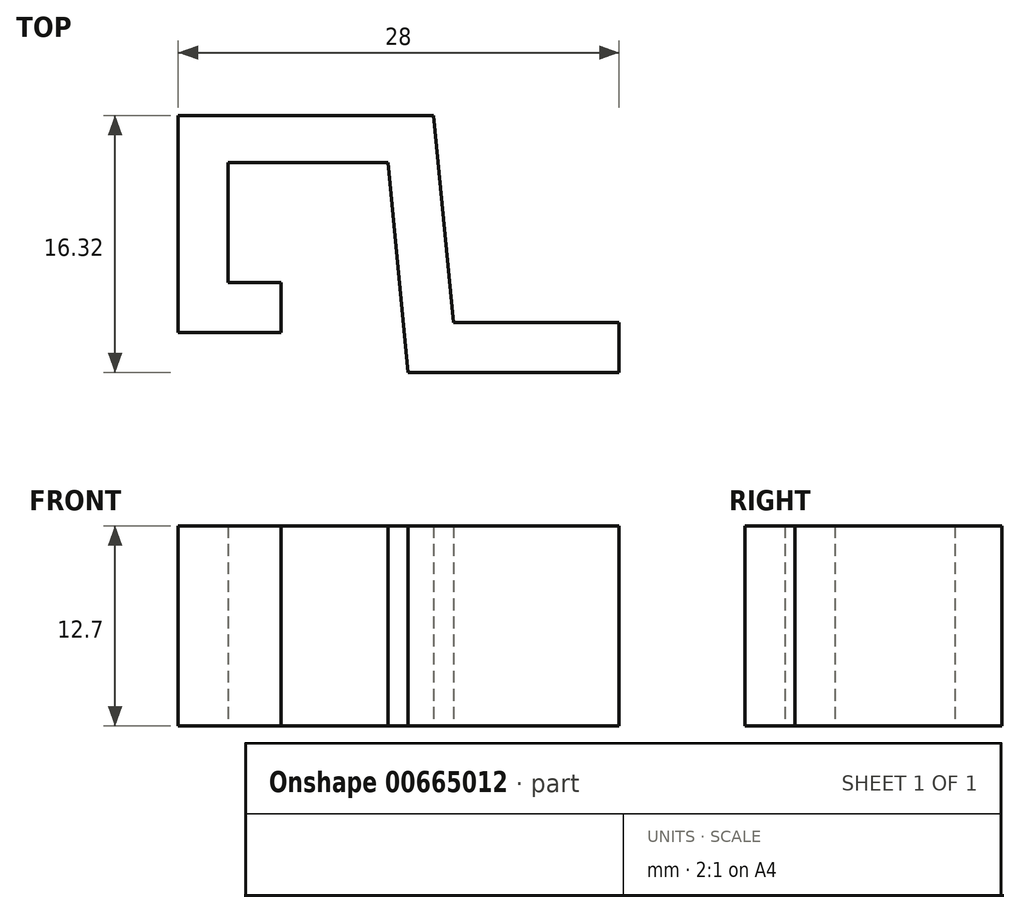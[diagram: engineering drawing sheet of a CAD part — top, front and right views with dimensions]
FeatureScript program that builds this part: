
annotation { "Feature Type Name" : "Feature", "Feature Type Description" : "" }
export const myFeature = defineFeature(function(context is Context, id is Id, definition is map)
    precondition{}
    {
        {
            var Q0;
            Q0=qCreatedBy(makeId("Top.planeOp"),FACE);
            var sketch = newSketch(context, id + "F0", { "sketchPlane" : qUnion([Q0])});
            skLineSegment(sketch, "E0.bottom", {"start": v(-13.34, 2.98) * mm, "end": v(-10.16, 2.98) * mm});
            skLineSegment(sketch, "E0.top", {"start": v(-13.34, -10.8) * mm, "end": v(-10.16, -10.8) * mm});
            skLineSegment(sketch, "E0.left", {"start": v(-13.34, 2.98) * mm, "end": v(-13.34, -10.8) * mm});
            skLineSegment(sketch, "E0.right", {"start": v(-10.16, 2.98) * mm, "end": v(-10.16, -10.8) * mm});
            skLineSegment(sketch, "E1.bottom", {"start": v(-6.79, -7.62) * mm, "end": v(-13.34, -7.62) * mm});
            skLineSegment(sketch, "E1.top", {"start": v(-6.79, -10.8) * mm, "end": v(-13.34, -10.8) * mm});
            skLineSegment(sketch, "E1.left", {"start": v(-6.79, -7.62) * mm, "end": v(-6.79, -10.8) * mm});
            skLineSegment(sketch, "E1.right", {"start": v(-13.34, -7.62) * mm, "end": v(-13.34, -10.8) * mm});
            skLineSegment(sketch, "E2.bottom", {"start": v(-13.34, 2.98) * mm, "end": v(2.9, 2.98) * mm});
            skLineSegment(sketch, "E2.top", {"start": v(-13.34, 0) * mm, "end": v(3.18, 0) * mm});
            skLineSegment(sketch, "E2.left", {"start": v(-13.34, 2.98) * mm, "end": v(-13.34, 0) * mm});
            skLineSegment(sketch, "E2.right", {"start": v(2.9, 2.98) * mm, "end": v(3.18, 0) * mm});
            skLineSegment(sketch, "E3.bottom", {"start": v(1.27, -10.16) * mm, "end": v(14.67, -10.16) * mm});
            skLineSegment(sketch, "E3.top", {"start": v(1.27, -13.34) * mm, "end": v(14.67, -13.34) * mm});
            skLineSegment(sketch, "E3.left", {"start": v(1.27, -10.16) * mm, "end": v(1.27, -13.34) * mm});
            skLineSegment(sketch, "E3.right", {"start": v(14.67, -10.16) * mm, "end": v(14.67, -13.34) * mm});
            skLineSegment(sketch, "E4", {"start": v(0, 0) * mm, "end": v(1.27, -13.34) * mm});
            skLineSegment(sketch, "E5", {"start": v(3.18, 0) * mm, "end": v(4.44, -13.34) * mm});
            skSolve(sketch);
        }
        {
            var Q0;
            Q0 = qSketchRegion(id + "F0", true);
            extrude(context, id + "F1", {"entities" : qUnion([Q0]), "depth" : 12.7 * mm, "offsetDistance" : 25.4 * mm});
        }
    });
